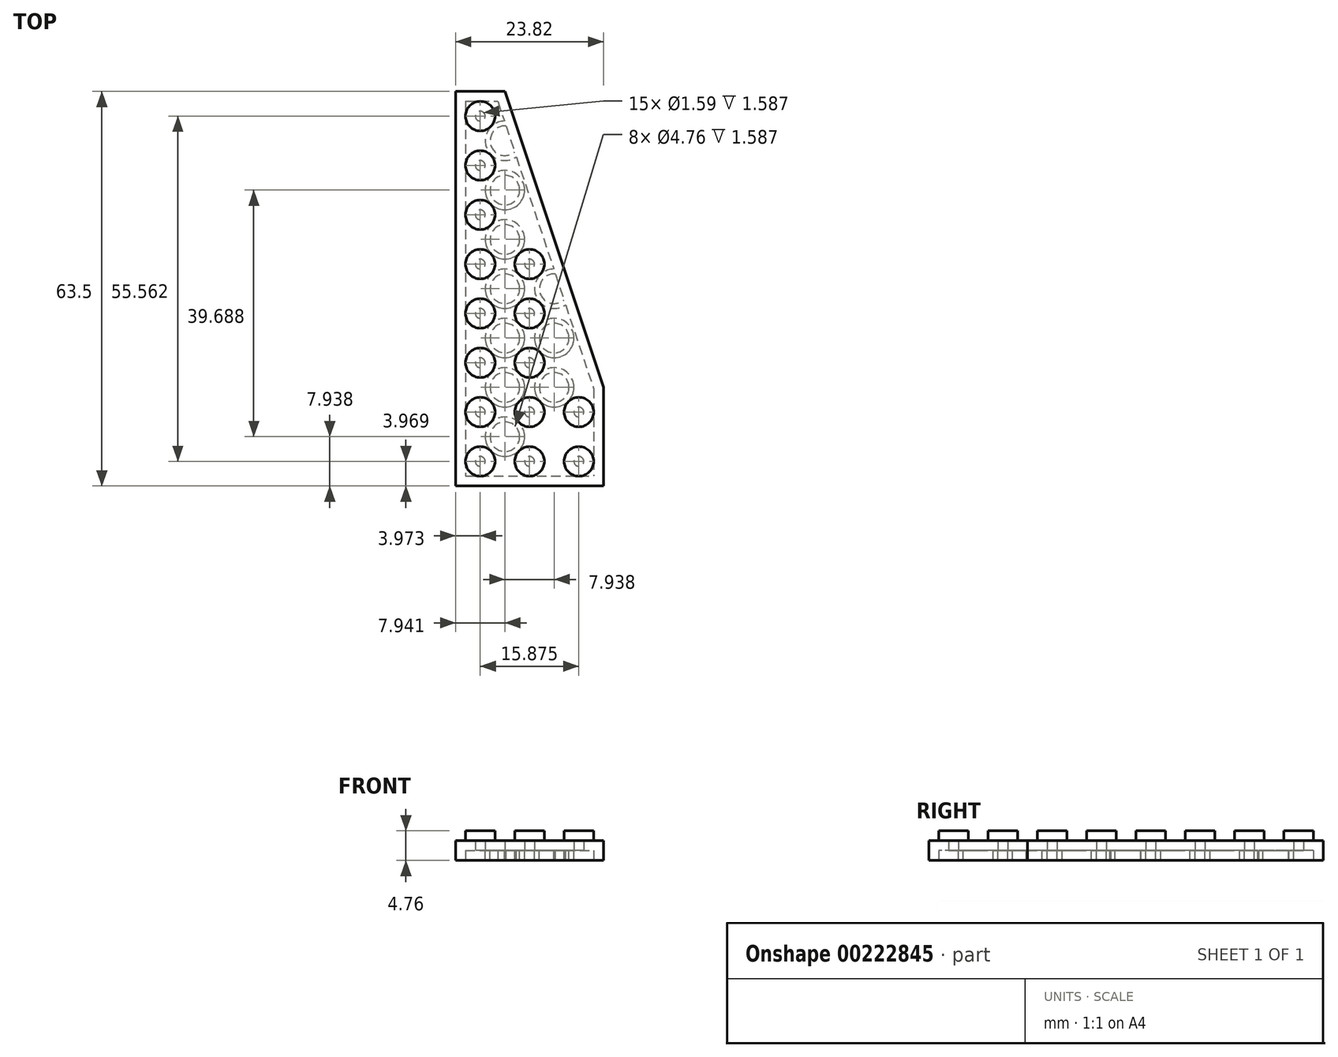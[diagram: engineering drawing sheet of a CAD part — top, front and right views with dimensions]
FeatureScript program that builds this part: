
annotation { "Feature Type Name" : "Feature", "Feature Type Description" : "" }
export const myFeature = defineFeature(function(context is Context, id is Id, definition is map)
    precondition{}
    {
        {
            var Q0;
            Q0=qCreatedBy(makeId("Top.planeOp"),FACE);
            var sketch = newSketch(context, id + "F0", { "sketchPlane" : qUnion([Q0])});
            skLineSegment(sketch, "E0.bottom", {"start": v(-11.9, 31.75) * mm, "end": v(11.9, 31.75) * mm});
            skLineSegment(sketch, "E0.top", {"start": v(-11.9, -31.75) * mm, "end": v(11.9, -31.75) * mm});
            skLineSegment(sketch, "E0.left", {"start": v(-11.9, 31.75) * mm, "end": v(-11.9, -31.75) * mm});
            skLineSegment(sketch, "E0.right", {"start": v(11.9, 31.75) * mm, "end": v(11.9, -31.75) * mm});
            skPoint(sketch, "E0.middle", {"position": v(0, 0) * mm});
            skPoint(sketch, "E1", {"position": v(11.9, -15.88) * mm});
            skPoint(sketch, "E2", {"position": v(-3.97, 31.75) * mm});
            skLineSegment(sketch, "E3", {"start": v(-3.97, 31.75) * mm, "end": v(11.9, -15.88) * mm});
            skCircle(sketch, "E4", {"center": v(-7.94, -27.78) * mm, "radius": 2.38 * mm});
            skCircle(sketch, "E5.0.1.0", {"center": v(-7.94, -19.84) * mm, "radius": 2.38 * mm});
            skCircle(sketch, "E5.1.0.0", {"center": v(0, -27.78) * mm, "radius": 2.38 * mm});
            skCircle(sketch, "E5.1.1.0", {"center": v(0, -19.84) * mm, "radius": 2.38 * mm});
            skCircle(sketch, "E5.2.0.0", {"center": v(7.94, -27.78) * mm, "radius": 2.38 * mm});
            skCircle(sketch, "E5.2.1.0", {"center": v(7.94, -19.84) * mm, "radius": 2.38 * mm});
            skLineSegment(sketch, "E5.direction1", {"start": v(-7.94, -27.78) * mm, "end": v(0, -27.78) * mm, "construction": true});
            skLineSegment(sketch, "E5.direction2", {"start": v(-7.94, -27.78) * mm, "end": v(-7.94, -19.84) * mm, "construction": true});
            skCircle(sketch, "E6.0.1.0", {"center": v(-7.94, -11.9) * mm, "radius": 2.38 * mm});
            skCircle(sketch, "E6.0.2.0", {"center": v(-7.94, -3.97) * mm, "radius": 2.38 * mm});
            skCircle(sketch, "E6.0.3.0", {"center": v(-7.94, 3.97) * mm, "radius": 2.38 * mm});
            skCircle(sketch, "E6.0.4.0", {"center": v(-7.94, 11.9) * mm, "radius": 2.38 * mm});
            skCircle(sketch, "E6.0.5.0", {"center": v(-7.94, 19.84) * mm, "radius": 2.38 * mm});
            skCircle(sketch, "E6.0.6.0", {"center": v(-7.94, 27.78) * mm, "radius": 2.38 * mm});
            skLineSegment(sketch, "E6.direction1", {"start": v(-7.94, -19.84) * mm, "end": v(17.46, -19.84) * mm, "construction": true});
            skLineSegment(sketch, "E6.direction2", {"start": v(-7.94, -19.84) * mm, "end": v(-7.94, -11.9) * mm, "construction": true});
            skCircle(sketch, "E7.0.1.0", {"center": v(0, -11.9) * mm, "radius": 2.38 * mm});
            skCircle(sketch, "E7.0.2.0", {"center": v(0, -3.97) * mm, "radius": 2.38 * mm});
            skCircle(sketch, "E7.0.3.0", {"center": v(0, 3.97) * mm, "radius": 2.38 * mm});
            skLineSegment(sketch, "E7.direction1", {"start": v(0, -19.84) * mm, "end": v(25.4, -19.84) * mm, "construction": true});
            skLineSegment(sketch, "E7.direction2", {"start": v(0, -19.84) * mm, "end": v(0, -11.9) * mm, "construction": true});
            skSolve(sketch);
        }
        {
            var Q0;
            {var subQ3=sQuery(id+"F0.wireOp",EDGE,"E0.top");Q0=makeQuery(id+"F0.imprint","IMPRINT",FACE,{"disambiguationData":[TD([[makeQuery(id+"F0.imprint","IMPRINT",EDGE,{"derivedFrom":subQ3}),1.0]])]});}
            extrude(context, id + "F1", {"entities" : qUnion([Q0]), "depth" : 3.17 * mm});
        }
        {
            var Q0;
            Q0=makeQuery(id+"F0.imprint","IMPRINT",FACE,{"disambiguationData":[TD([[makeQuery(id+"F0.imprint","IMPRINT",EDGE,{"derivedFrom":sQuery(id+"F0.wireOp",EDGE,"E6.0.6.0")}),1.0]])]});
            var Q1;
            Q1=makeQuery(id+"F0.imprint","IMPRINT",FACE,{"disambiguationData":[TD([[makeQuery(id+"F0.imprint","IMPRINT",EDGE,{"derivedFrom":sQuery(id+"F0.wireOp",EDGE,"E6.0.5.0")}),1.0]])]});
            var Q2;
            Q2=makeQuery(id+"F0.imprint","IMPRINT",FACE,{"disambiguationData":[TD([[makeQuery(id+"F0.imprint","IMPRINT",EDGE,{"derivedFrom":sQuery(id+"F0.wireOp",EDGE,"E6.0.4.0")}),1.0]])]});
            var Q3;
            Q3=makeQuery(id+"F0.imprint","IMPRINT",FACE,{"disambiguationData":[TD([[makeQuery(id+"F0.imprint","IMPRINT",EDGE,{"derivedFrom":sQuery(id+"F0.wireOp",EDGE,"E6.0.3.0")}),1.0]])]});
            var Q4;
            Q4=makeQuery(id+"F0.imprint","IMPRINT",FACE,{"disambiguationData":[TD([[makeQuery(id+"F0.imprint","IMPRINT",EDGE,{"derivedFrom":sQuery(id+"F0.wireOp",EDGE,"E6.0.2.0")}),1.0]])]});
            var Q5;
            Q5=makeQuery(id+"F0.imprint","IMPRINT",FACE,{"disambiguationData":[TD([[makeQuery(id+"F0.imprint","IMPRINT",EDGE,{"derivedFrom":sQuery(id+"F0.wireOp",EDGE,"E6.0.1.0")}),1.0]])]});
            var Q6;
            Q6=makeQuery(id+"F0.imprint","IMPRINT",FACE,{"disambiguationData":[TD([[makeQuery(id+"F0.imprint","IMPRINT",EDGE,{"derivedFrom":sQuery(id+"F0.wireOp",EDGE,"E5.0.1.0")}),1.0]])]});
            var Q7;
            Q7=makeQuery(id+"F0.imprint","IMPRINT",FACE,{"disambiguationData":[TD([[makeQuery(id+"F0.imprint","IMPRINT",EDGE,{"derivedFrom":sQuery(id+"F0.wireOp",EDGE,"E4")}),1.0]])]});
            var Q8;
            Q8=makeQuery(id+"F0.imprint","IMPRINT",FACE,{"disambiguationData":[TD([[makeQuery(id+"F0.imprint","IMPRINT",EDGE,{"derivedFrom":sQuery(id+"F0.wireOp",EDGE,"E5.1.0.0")}),1.0]])]});
            var Q9;
            Q9=makeQuery(id+"F0.imprint","IMPRINT",FACE,{"disambiguationData":[TD([[makeQuery(id+"F0.imprint","IMPRINT",EDGE,{"derivedFrom":sQuery(id+"F0.wireOp",EDGE,"E5.1.1.0")}),1.0]])]});
            var Q10;
            Q10=makeQuery(id+"F0.imprint","IMPRINT",FACE,{"disambiguationData":[TD([[makeQuery(id+"F0.imprint","IMPRINT",EDGE,{"derivedFrom":sQuery(id+"F0.wireOp",EDGE,"E7.0.1.0")}),1.0]])]});
            var Q11;
            Q11=makeQuery(id+"F0.imprint","IMPRINT",FACE,{"disambiguationData":[TD([[makeQuery(id+"F0.imprint","IMPRINT",EDGE,{"derivedFrom":sQuery(id+"F0.wireOp",EDGE,"E7.0.2.0")}),1.0]])]});
            var Q12;
            Q12=makeQuery(id+"F0.imprint","IMPRINT",FACE,{"disambiguationData":[TD([[makeQuery(id+"F0.imprint","IMPRINT",EDGE,{"derivedFrom":sQuery(id+"F0.wireOp",EDGE,"E7.0.3.0")}),1.0]])]});
            var Q13;
            Q13=makeQuery(id+"F0.imprint","IMPRINT",FACE,{"disambiguationData":[TD([[makeQuery(id+"F0.imprint","IMPRINT",EDGE,{"derivedFrom":sQuery(id+"F0.wireOp",EDGE,"E5.2.1.0")}),1.0]])]});
            var Q14;
            Q14=makeQuery(id+"F0.imprint","IMPRINT",FACE,{"disambiguationData":[TD([[makeQuery(id+"F0.imprint","IMPRINT",EDGE,{"derivedFrom":sQuery(id+"F0.wireOp",EDGE,"E5.2.0.0")}),1.0]])]});
            extrude(context, id + "F2", {"entities" : qUnion([Q0, Q1, Q2, Q3, Q4, Q5, Q6, Q7, Q8, Q9, Q10, Q11, Q12, Q13, Q14]), "operationType" : NewBodyOperationType.ADD, "depth" : 4.76 * mm});
        }
        {
            var Q0;
            {var subQ0=sQuery(id+"F0.wireOp",EDGE,"E7.0.3.0");var subQ1=sQuery(id+"F0.wireOp",EDGE,"E7.0.2.0");var subQ2=sQuery(id+"F0.wireOp",EDGE,"E7.0.1.0");var subQ3=sQuery(id+"F0.wireOp",EDGE,"E6.0.6.0");var subQ4=sQuery(id+"F0.wireOp",EDGE,"E6.0.5.0");var subQ5=sQuery(id+"F0.wireOp",EDGE,"E6.0.4.0");var subQ6=sQuery(id+"F0.wireOp",EDGE,"E6.0.3.0");var subQ7=sQuery(id+"F0.wireOp",EDGE,"E6.0.2.0");var subQ8=sQuery(id+"F0.wireOp",EDGE,"E6.0.1.0");var subQ9=sQuery(id+"F0.wireOp",EDGE,"E5.2.1.0");var subQ10=sQuery(id+"F0.wireOp",EDGE,"E5.2.0.0");var subQ11=sQuery(id+"F0.wireOp",EDGE,"E5.1.1.0");var subQ12=sQuery(id+"F0.wireOp",EDGE,"E5.1.0.0");var subQ13=sQuery(id+"F0.wireOp",EDGE,"E5.0.1.0");var subQ14=sQuery(id+"F0.wireOp",EDGE,"E4");Q0=makeQuery(id+"F2.boolean.opBoolean","MERGE",FACE,{"derivedFrom":[makeQuery(id+"F1.opExtrude","CAP_FACE",FACE,{"disambiguationData":[OSD([sQuery(id+"F0.wireOp",EDGE,"E0.bottom"),sQuery(id+"F0.wireOp",EDGE,"E0.top"),sQuery(id+"F0.wireOp",EDGE,"E0.left"),sQuery(id+"F0.wireOp",EDGE,"E0.right"),sQuery(id+"F0.wireOp",EDGE,"E3"),subQ14,subQ13,subQ12,subQ11,subQ10,subQ9,subQ8,subQ7,subQ6,subQ5,subQ4,subQ3,subQ2,subQ1,subQ0])],"isStart":true}),makeQuery(id+"F2.opExtrude","CAP_FACE",FACE,{"disambiguationData":[OSD([subQ14])],"isStart":true}),makeQuery(id+"F2.opExtrude","CAP_FACE",FACE,{"disambiguationData":[OSD([subQ13])],"isStart":true}),makeQuery(id+"F2.opExtrude","CAP_FACE",FACE,{"disambiguationData":[OSD([subQ12])],"isStart":true}),makeQuery(id+"F2.opExtrude","CAP_FACE",FACE,{"disambiguationData":[OSD([subQ11])],"isStart":true}),makeQuery(id+"F2.opExtrude","CAP_FACE",FACE,{"disambiguationData":[OSD([subQ10])],"isStart":true}),makeQuery(id+"F2.opExtrude","CAP_FACE",FACE,{"disambiguationData":[OSD([subQ9])],"isStart":true}),makeQuery(id+"F2.opExtrude","CAP_FACE",FACE,{"disambiguationData":[OSD([subQ8])],"isStart":true}),makeQuery(id+"F2.opExtrude","CAP_FACE",FACE,{"disambiguationData":[OSD([subQ7])],"isStart":true}),makeQuery(id+"F2.opExtrude","CAP_FACE",FACE,{"disambiguationData":[OSD([subQ6])],"isStart":true}),makeQuery(id+"F2.opExtrude","CAP_FACE",FACE,{"disambiguationData":[OSD([subQ5])],"isStart":true}),makeQuery(id+"F2.opExtrude","CAP_FACE",FACE,{"disambiguationData":[OSD([subQ4])],"isStart":true}),makeQuery(id+"F2.opExtrude","CAP_FACE",FACE,{"disambiguationData":[OSD([subQ3])],"isStart":true}),makeQuery(id+"F2.opExtrude","CAP_FACE",FACE,{"disambiguationData":[OSD([subQ2])],"isStart":true}),makeQuery(id+"F2.opExtrude","CAP_FACE",FACE,{"disambiguationData":[OSD([subQ1])],"isStart":true}),makeQuery(id+"F2.opExtrude","CAP_FACE",FACE,{"disambiguationData":[OSD([subQ0])],"isStart":true})]});}
            shell(context, id + "F3", {"entities" : qUnion([Q0]), "thickness" : 1.59 * mm});
        }
        {
            var Q0;
            Q0=makeQuery(id+"F3.opShell","OFFSET_FACE",FACE,{"disambiguationData":[OSD([sQuery(id+"F0.wireOp",EDGE,"E0.bottom"),sQuery(id+"F0.wireOp",EDGE,"E0.top"),sQuery(id+"F0.wireOp",EDGE,"E0.left"),sQuery(id+"F0.wireOp",EDGE,"E0.right"),sQuery(id+"F0.wireOp",EDGE,"E3"),sQuery(id+"F0.wireOp",EDGE,"E4"),sQuery(id+"F0.wireOp",EDGE,"E5.0.1.0"),sQuery(id+"F0.wireOp",EDGE,"E5.1.0.0"),sQuery(id+"F0.wireOp",EDGE,"E5.1.1.0"),sQuery(id+"F0.wireOp",EDGE,"E5.2.0.0"),sQuery(id+"F0.wireOp",EDGE,"E5.2.1.0"),sQuery(id+"F0.wireOp",EDGE,"E6.0.1.0"),sQuery(id+"F0.wireOp",EDGE,"E6.0.2.0"),sQuery(id+"F0.wireOp",EDGE,"E6.0.3.0"),sQuery(id+"F0.wireOp",EDGE,"E6.0.4.0"),sQuery(id+"F0.wireOp",EDGE,"E6.0.5.0"),sQuery(id+"F0.wireOp",EDGE,"E6.0.6.0"),sQuery(id+"F0.wireOp",EDGE,"E7.0.1.0"),sQuery(id+"F0.wireOp",EDGE,"E7.0.2.0"),sQuery(id+"F0.wireOp",EDGE,"E7.0.3.0")])]});
            var sketch = newSketch(context, id + "F4", { "sketchPlane" : qUnion([Q0])});
            skLineSegment(sketch, "E8", {"start": v(7.94, 19.84) * mm, "end": v(0, 27.78) * mm});
            skCircle(sketch, "E9", {"center": v(3.97, 23.81) * mm, "radius": 3.18 * mm});
            skCircle(sketch, "E10.0", {"center": v(3.97, 23.81) * mm, "radius": 2.38 * mm});
            skCircle(sketch, "E11.0.1.0", {"center": v(3.97, 15.88) * mm, "radius": 3.18 * mm});
            skCircle(sketch, "E11.0.1.1", {"center": v(3.97, 15.88) * mm, "radius": 2.38 * mm});
            skCircle(sketch, "E11.0.2.0", {"center": v(3.97, 7.94) * mm, "radius": 3.18 * mm});
            skCircle(sketch, "E11.0.2.1", {"center": v(3.97, 7.94) * mm, "radius": 2.38 * mm});
            skCircle(sketch, "E11.0.3.0", {"center": v(3.97, 0) * mm, "radius": 3.18 * mm});
            skCircle(sketch, "E11.0.3.1", {"center": v(3.97, 0) * mm, "radius": 2.38 * mm});
            skCircle(sketch, "E11.0.4.0", {"center": v(3.97, -7.94) * mm, "radius": 3.18 * mm});
            skCircle(sketch, "E11.0.4.1", {"center": v(3.97, -7.94) * mm, "radius": 2.38 * mm});
            skCircle(sketch, "E11.0.5.0", {"center": v(3.97, -15.87) * mm, "radius": 3.18 * mm});
            skCircle(sketch, "E11.0.5.1", {"center": v(3.97, -15.87) * mm, "radius": 2.38 * mm});
            skCircle(sketch, "E11.0.6.0", {"center": v(3.97, -23.81) * mm, "radius": 3.18 * mm});
            skCircle(sketch, "E11.0.6.1", {"center": v(3.97, -23.81) * mm, "radius": 2.38 * mm});
            skCircle(sketch, "E11.1.0.0", {"center": v(-3.97, 23.81) * mm, "radius": 3.18 * mm});
            skCircle(sketch, "E11.1.0.1", {"center": v(-3.97, 23.81) * mm, "radius": 2.38 * mm});
            skCircle(sketch, "E11.1.1.0", {"center": v(-3.97, 15.88) * mm, "radius": 3.18 * mm});
            skCircle(sketch, "E11.1.1.1", {"center": v(-3.97, 15.88) * mm, "radius": 2.38 * mm});
            skCircle(sketch, "E11.1.2.0", {"center": v(-3.97, 7.94) * mm, "radius": 3.18 * mm});
            skCircle(sketch, "E11.1.2.1", {"center": v(-3.97, 7.94) * mm, "radius": 2.38 * mm});
            skCircle(sketch, "E11.1.3.0", {"center": v(-3.97, 0) * mm, "radius": 3.18 * mm});
            skCircle(sketch, "E11.1.3.1", {"center": v(-3.97, 0) * mm, "radius": 2.38 * mm});
            skCircle(sketch, "E11.1.4.0", {"center": v(-3.97, -7.94) * mm, "radius": 3.18 * mm});
            skCircle(sketch, "E11.1.4.1", {"center": v(-3.97, -7.94) * mm, "radius": 2.38 * mm});
            skCircle(sketch, "E11.1.5.0", {"center": v(-3.97, -15.87) * mm, "radius": 3.18 * mm});
            skCircle(sketch, "E11.1.5.1", {"center": v(-3.97, -15.87) * mm, "radius": 2.38 * mm});
            skCircle(sketch, "E11.1.6.0", {"center": v(-3.97, -23.81) * mm, "radius": 3.18 * mm});
            skCircle(sketch, "E11.1.6.1", {"center": v(-3.97, -23.81) * mm, "radius": 2.38 * mm});
            skLineSegment(sketch, "E11.direction1", {"start": v(3.97, 23.81) * mm, "end": v(-3.97, 23.81) * mm, "construction": true});
            skLineSegment(sketch, "E11.direction2", {"start": v(3.97, 23.81) * mm, "end": v(3.97, 15.88) * mm, "construction": true});
            skSolve(sketch);
        }
        {
            var Q0;
            {var subQ0=sQuery(id+"F4.wireOp",EDGE,"E9");var subQ1=sQuery(id+"F4.wireOp",EDGE,"E8");var subQ2=makeQuery(id+"F4.imprint","INTERSECT",VERTEX,{"disambiguationData":[OD(0.0)],"derivedFrom":[subQ1,subQ0]});Q0=makeQuery(id+"F4.imprint","IMPRINT",FACE,{"disambiguationData":[TD([[makeQuery(id+"F4.imprint","IMPRINT",EDGE,{"disambiguationData":[TD([[subQ2,-1.0]])],"derivedFrom":subQ1}),-1.0]])]});}
            var Q1;
            {var subQ0=sQuery(id+"F4.wireOp",EDGE,"E9");var subQ1=sQuery(id+"F4.wireOp",EDGE,"E8");var subQ2=makeQuery(id+"F4.imprint","INTERSECT",VERTEX,{"disambiguationData":[OD(0.0)],"derivedFrom":[subQ1,subQ0]});Q1=makeQuery(id+"F4.imprint","IMPRINT",FACE,{"disambiguationData":[TD([[makeQuery(id+"F4.imprint","IMPRINT",EDGE,{"disambiguationData":[TD([[subQ2,-1.0]])],"derivedFrom":subQ1}),1.0]])]});}
            var Q2;
            Q2=makeQuery(id+"F4.imprint","IMPRINT",FACE,{"disambiguationData":[TD([[makeQuery(id+"F4.imprint","IMPRINT",EDGE,{"derivedFrom":sQuery(id+"F4.wireOp",EDGE,"E11.0.1.0")}),1.0]])]});
            var Q3;
            Q3=makeQuery(id+"F4.imprint","IMPRINT",FACE,{"disambiguationData":[TD([[makeQuery(id+"F4.imprint","IMPRINT",EDGE,{"derivedFrom":sQuery(id+"F4.wireOp",EDGE,"E11.0.2.0")}),1.0]])]});
            var Q4;
            {var subQ0=sQuery(id+"F4.wireOp",EDGE,"E11.0.3.0");var subQ1=sQuery(id+"F0.wireOp",EDGE,"E3");var subQ2=makeQuery(id+"F3.opShell","OFFSET_EDGE",EDGE,{"disambiguationData":[OSD([subQ1]),TDD([makeQuery(id+"F1.opExtrude","CAP_EDGE",EDGE,{"disambiguationData":[OSD([subQ1])],"isStart":false})])]});var subQ3=makeQuery(id+"F4.imprint","INTERSECT",VERTEX,{"disambiguationData":[OD(0.0)],"derivedFrom":[subQ2,subQ0]});Q4=makeQuery(id+"F4.imprint","IMPRINT",FACE,{"disambiguationData":[TD([[makeQuery(id+"F4.imprint","IMPRINT",EDGE,{"disambiguationData":[TD([[subQ3,-1.0]])],"derivedFrom":subQ0}),1.0]])]});}
            var Q5;
            Q5=makeQuery(id+"F4.imprint","IMPRINT",FACE,{"disambiguationData":[TD([[makeQuery(id+"F4.imprint","IMPRINT",EDGE,{"derivedFrom":sQuery(id+"F4.wireOp",EDGE,"E11.1.5.0")}),1.0]])]});
            var Q6;
            {var subQ0=sQuery(id+"F4.wireOp",EDGE,"E11.1.6.0");var subQ1=sQuery(id+"F0.wireOp",EDGE,"E3");var subQ2=makeQuery(id+"F3.opShell","OFFSET_EDGE",EDGE,{"disambiguationData":[OSD([subQ1]),TDD([makeQuery(id+"F1.opExtrude","CAP_EDGE",EDGE,{"disambiguationData":[OSD([subQ1])],"isStart":false})])]});var subQ3=makeQuery(id+"F4.imprint","INTERSECT",VERTEX,{"disambiguationData":[OD(0.0)],"derivedFrom":[subQ2,subQ0]});Q6=makeQuery(id+"F4.imprint","IMPRINT",FACE,{"disambiguationData":[TD([[makeQuery(id+"F4.imprint","IMPRINT",EDGE,{"disambiguationData":[TD([[subQ3,1.0]])],"derivedFrom":subQ0}),1.0]])]});}
            var Q7;
            Q7=makeQuery(id+"F4.imprint","IMPRINT",FACE,{"disambiguationData":[TD([[makeQuery(id+"F4.imprint","IMPRINT",EDGE,{"derivedFrom":sQuery(id+"F4.wireOp",EDGE,"E11.1.4.0")}),1.0]])]});
            var Q8;
            Q8=makeQuery(id+"F4.imprint","IMPRINT",FACE,{"disambiguationData":[TD([[makeQuery(id+"F4.imprint","IMPRINT",EDGE,{"derivedFrom":sQuery(id+"F4.wireOp",EDGE,"E11.1.3.0")}),1.0]])]});
            var Q9;
            Q9=makeQuery(id+"F4.imprint","IMPRINT",FACE,{"disambiguationData":[TD([[makeQuery(id+"F4.imprint","IMPRINT",EDGE,{"derivedFrom":sQuery(id+"F4.wireOp",EDGE,"E11.1.2.0")}),1.0]])]});
            var Q10;
            Q10=makeQuery(id+"F4.imprint","IMPRINT",FACE,{"disambiguationData":[TD([[makeQuery(id+"F4.imprint","IMPRINT",EDGE,{"derivedFrom":sQuery(id+"F4.wireOp",EDGE,"E11.1.1.0")}),1.0]])]});
            var Q11;
            Q11=makeQuery(id+"F4.imprint","IMPRINT",FACE,{"disambiguationData":[TD([[makeQuery(id+"F4.imprint","IMPRINT",EDGE,{"derivedFrom":sQuery(id+"F4.wireOp",EDGE,"E11.1.0.0")}),1.0]])]});
            extrude(context, id + "F5", {"entities" : qUnion([Q0, Q1, Q2, Q3, Q4, Q5, Q6, Q7, Q8, Q9, Q10, Q11]), "operationType" : NewBodyOperationType.ADD, "depth" : 1.59 * mm});
        }
    });
